# Revit family: STORA-LK-I-D1500-8xx-OSx
name_source: partatom
category: Oprawy oświetleniowe
revit_build: Autodesk Revit 2017 (Build: 20190508_0315(x64)
units: mm (PartAtom-declared; Revit-internal decimal feet)

## family parameters
Numer OmniClass = 23.80.70.11
Obiekt nadrzędny = Powierzchnia
Punkt obliczania pomieszczeń = Nie
Tnij formami wycięć po wczytaniu = Nie
Typ części = Normalny
Tytuł OmniClass = Luminaries for Internal Lighting
Współdzielony = Nie
Wymiar okrągłego złącza = Użyj średnicy
Źródło światła = Tak

## types (4) — shared parameters
Emituj kształt widoczny w renderingu = Nie
Emituj ze średnicy okręgu = 1485 mm  [stored 4.87205 ft]
Filtr koloru = 16777215
Kod zespołu = D5020200
Lampa = LED
Obciążenie pozorne = 156 VA
Odchylenie kierunku = 90.00°
Plik sieci fotometrycznej = STORA-LK-I-LED D0950840 OS.IES
Producent = RIDI Leuchten GmbH
URL = www.spectral-lighting.com
Zmiana temperatury barwowej przyciemniania lampy = <Brak>
brand = Spectral
conformity mark = CE
electrical safety class = 1
height = 100 mm  [stored 0.328084 ft]
ingress protection (IP) code = IP20
length = 1500 mm  [stored 4.92126 ft]
nominal frequency = 50-60Hz
nominal voltage = 230
rated input power = 156
voltage type (AC, DC, UC) = AC
weight = 23,5
width = 1500 mm  [stored 4.92126 ft]
zero-valued in all types: Domyślna rzędna

## per-type parameters (varying)
| type | Model |
| STORA-LK-I D1500/830 OS | SPC0620022 |
| STORA-LK-I D1500/830 OS-DA | SPC0630022 |
| STORA-LK-I D1500/840 OS | SPC0620018 |
| STORA-LK-I D1500/840 OS-DA | SPC0630018 |

note: column(s) folded — value = type name in every type: product name

note: [stored X ft] marks values corroborated as IEEE doubles in the binary element streams (Revit-internal decimal feet)
